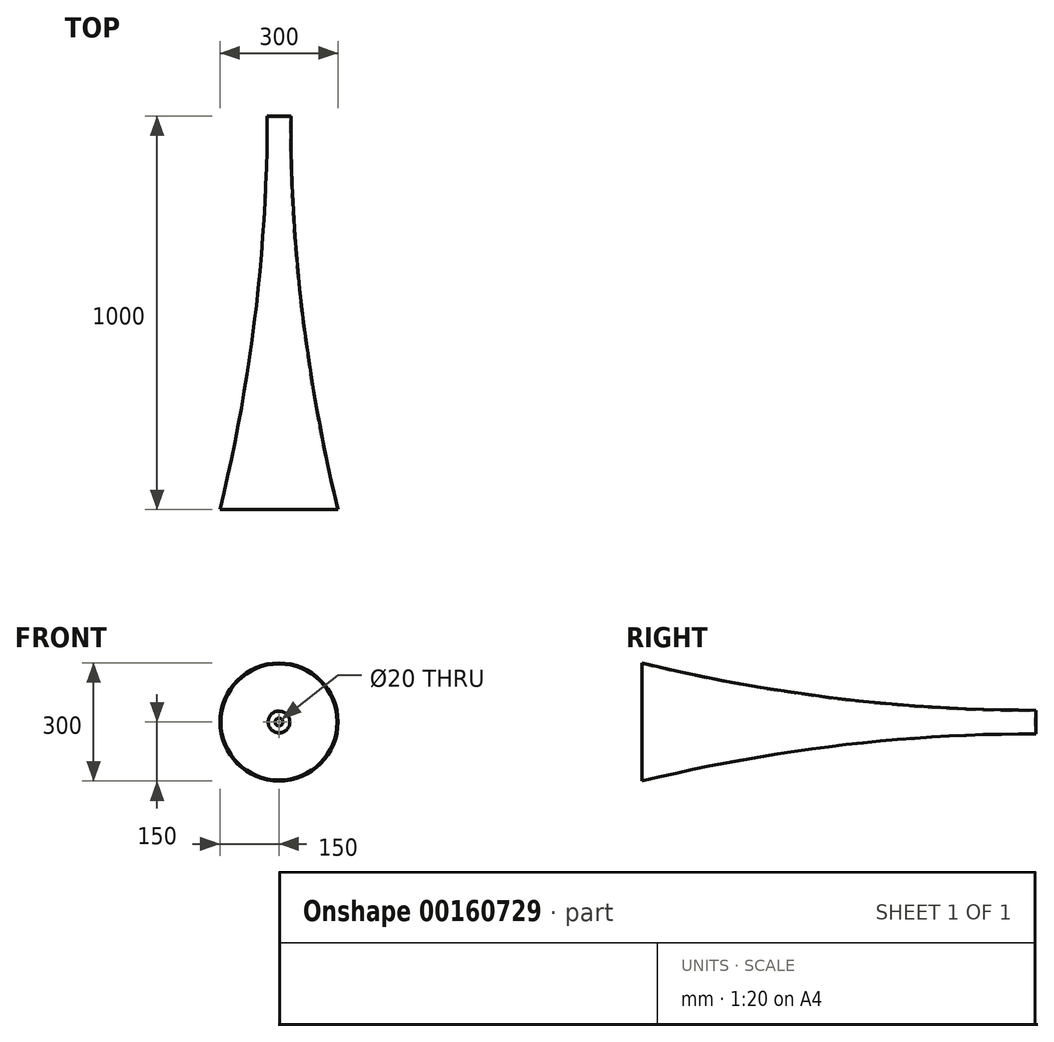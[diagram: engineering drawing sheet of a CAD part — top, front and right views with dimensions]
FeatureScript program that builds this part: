
annotation { "Feature Type Name" : "Feature", "Feature Type Description" : "" }
export const myFeature = defineFeature(function(context is Context, id is Id, definition is map)
    precondition{}
    {
        {
            var Q0;
            Q0=qCreatedBy(makeId("Front.planeOp"),FACE);
            cPlane(context, id + "F0", {"entities" : qUnion([Q0]), "cplaneType" : CPlaneType.OFFSET, "offset" : 1000 * mm, "width" : 152.4 * mm, "height" : 152.4 * mm});
        }
        {
            var Q0;
            Q0=qCreatedBy(makeId("Front.planeOp"),FACE);
            var sketch = newSketch(context, id + "F1", { "sketchPlane" : qUnion([Q0])});
            skCircle(sketch, "E0", {"center": v(0, 0) * mm, "radius": 30 * mm});
            skSolve(sketch);
        }
        {
            var Q0;
            Q0=qCreatedBy(id+"F0.planeOp",FACE);
            var sketch = newSketch(context, id + "F2", { "sketchPlane" : qUnion([Q0])});
            skCircle(sketch, "E1", {"center": v(0, 0) * mm, "radius": 150 * mm});
            skSolve(sketch);
        }
        {
            var Q0;
            Q0=qCreatedBy(makeId("Right.planeOp"),FACE);
            var sketch = newSketch(context, id + "F3", { "sketchPlane" : qUnion([Q0])});
            skArc(sketch, "E2", {"start": v(-1000, 150) * mm, "mid": v(-503.59, 60.1) * mm, "end": v(0, 30) * mm});
            skSolve(sketch);
        }
        {
            var Q0;
            Q0=makeQuery(id+"F1.imprint","IMPRINT",FACE,{"disambiguationData":[TD([[makeQuery(id+"F1.imprint","IMPRINT",EDGE,{"derivedFrom":sQuery(id+"F1.wireOp",EDGE,"E0")}),1.0]])]});
            var Q1;
            Q1=makeQuery(id+"F2.imprint","IMPRINT",FACE,{"disambiguationData":[TD([[makeQuery(id+"F2.imprint","IMPRINT",EDGE,{"derivedFrom":sQuery(id+"F2.wireOp",EDGE,"E1")}),1.0]])]});
            var Q2;
            Q2=sQuery(id+"F3.wireOp",EDGE,"E2");
            loft(context, id + "F4", {"addGuides" : true, "sheetProfilesArray" : [{ "sheetProfileEntities" : qUnion([Q0]) }, { "sheetProfileEntities" : qUnion([Q1]) }], "guidesArray" : [{ "guideEntities" : qUnion([Q2]), "guideDerivativeType" : LoftGuideDerivativeType.DEFAULT, "guideDerivativeMagnitude" : 1 }]});
        }
        {
            var Q0;
            Q0=makeQuery(id+"F4.opLoft","CAP_FACE",FACE,{"disambiguationData":[OSD([makeQuery(id+"F2.imprint","IMPRINT",FACE,{"disambiguationData":[TD([[makeQuery(id+"F2.imprint","IMPRINT",EDGE,{"derivedFrom":sQuery(id+"F2.wireOp",EDGE,"E1")}),1.0]])]})])],"isStart":true});
            shell(context, id + "F5", {"entities" : qUnion([Q0]), "thickness" : 2.5 * mm});
        }
        {
            var Q0;
            Q0=qCreatedBy(makeId("Front.planeOp"),FACE);
            var sketch = newSketch(context, id + "F6", { "sketchPlane" : qUnion([Q0])});
            skCircle(sketch, "E3", {"center": v(0, 0) * mm, "radius": 10 * mm});
            skSolve(sketch);
        }
        {
            var Q0;
            Q0=makeQuery(id+"F6.imprint","IMPRINT",FACE,{"disambiguationData":[TD([[makeQuery(id+"F6.imprint","IMPRINT",EDGE,{"derivedFrom":sQuery(id+"F6.wireOp",EDGE,"E3")}),1.0]])]});
            extrude(context, id + "F7", {"entities" : qUnion([Q0]), "operationType" : NewBodyOperationType.REMOVE, "endBound" : BoundingType.UP_TO_NEXT, "depth" : 10 * mm});
        }
    });
